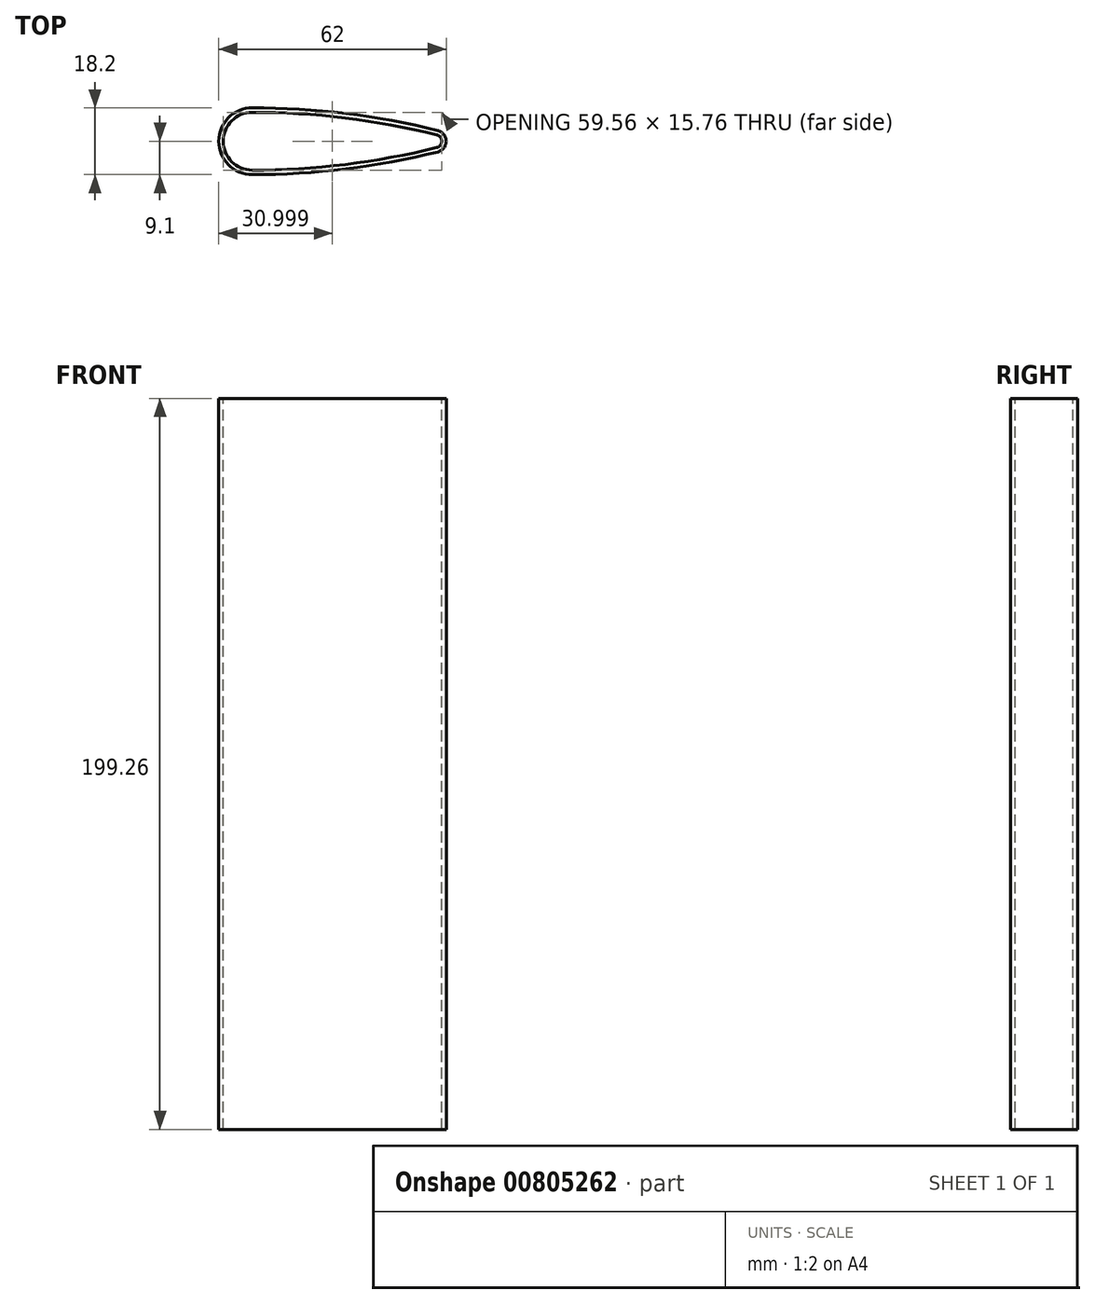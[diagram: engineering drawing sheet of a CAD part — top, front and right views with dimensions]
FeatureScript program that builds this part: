
annotation { "Feature Type Name" : "Feature", "Feature Type Description" : "" }
export const myFeature = defineFeature(function(context is Context, id is Id, definition is map)
    precondition{}
    {
        {
            var Q0;
            Q0=qCreatedBy(makeId("Front.planeOp"),FACE);
            var sketch = newSketch(context, id + "F0", { "sketchPlane" : qUnion([Q0])});
            skCircle(sketch, "E0", {"center": v(0, 0) * mm, "radius": 10 * mm});
            skLineSegment(sketch, "E1", {"start": v(-10, 0) * mm, "end": v(-10, 199.26) * mm});
            skSolve(sketch);
        }
        {
            var Q0;
            Q0=qCreatedBy(makeId("Top.planeOp"),FACE);
            var sketch = newSketch(context, id + "F1", { "sketchPlane" : qUnion([Q0])});
            skArc(sketch, "E2", {"start": v(-12.13, 9.1) * mm, "mid": v(-21.23, 0) * mm, "end": v(-12.13, -9.1) * mm});
            skLineSegment(sketch, "E3", {"start": v(-12.13, 0) * mm, "end": v(40.77, 0) * mm});
            skArc(sketch, "E4", {"start": v(38.5, -2.91) * mm, "mid": v(40.77, 0) * mm, "end": v(38.5, 2.91) * mm});
            skLineSegment(sketch, "E5", {"start": v(-12.13, 0) * mm, "end": v(-12.13, 9.1) * mm});
            skLineSegment(sketch, "E6", {"start": v(-12.13, 9.1) * mm, "end": v(10.82, 9.1) * mm});
            skArc(sketch, "E7", {"start": v(38.5, 2.91) * mm, "mid": v(13.37, 7.55) * mm, "end": v(-12.13, 9.1) * mm});
            skArc(sketch, "E8.MirrorCS", {"start": v(38.5, -2.91) * mm, "mid": v(13.37, -7.55) * mm, "end": v(-12.13, -9.1) * mm});
            skArc(sketch, "E9.0", {"start": v(38.2, 1.73) * mm, "mid": v(13.22, 6.34) * mm, "end": v(-12.13, 7.88) * mm});
            skArc(sketch, "E9.1", {"start": v(38.2, -1.73) * mm, "mid": v(13.22, -6.34) * mm, "end": v(-12.13, -7.88) * mm});
            skArc(sketch, "E9.2", {"start": v(-12.13, 7.88) * mm, "mid": v(-20.01, 0) * mm, "end": v(-12.13, -7.88) * mm});
            skArc(sketch, "E10", {"start": v(38.2, -1.73) * mm, "mid": v(39.55, 0) * mm, "end": v(38.2, 1.73) * mm});
            skSolve(sketch);
        }
        {
            var Q0;
            Q0=qCreatedBy(makeId("Top.planeOp"),FACE);
            var sketch = newSketch(context, id + "F2", { "sketchPlane" : qUnion([Q0])});
            skArc(sketch, "E11", {"start": v(-17.42, 11.17) * mm, "mid": v(-30.07, -1.48) * mm, "end": v(-17.42, -14.13) * mm});
            skLineSegment(sketch, "E12", {"start": v(-17.42, -1.48) * mm, "end": v(27.93, -1.48) * mm});
            skArc(sketch, "E13", {"start": v(25.9, -4.66) * mm, "mid": v(27.93, -1.48) * mm, "end": v(25.9, 1.7) * mm});
            skLineSegment(sketch, "E14", {"start": v(-17.42, -1.48) * mm, "end": v(-17.42, 11.17) * mm});
            skLineSegment(sketch, "E15", {"start": v(-17.42, 11.17) * mm, "end": v(-2.83, 11.17) * mm});
            skArc(sketch, "E16", {"start": v(25.9, 1.7) * mm, "mid": v(4.75, 8.77) * mm, "end": v(-17.42, 11.17) * mm});
            skArc(sketch, "E17.MirrorCS", {"start": v(25.9, -4.66) * mm, "mid": v(4.75, -11.74) * mm, "end": v(-17.42, -14.13) * mm});
            skArc(sketch, "E18.0", {"start": v(25.38, 0.59) * mm, "mid": v(4.49, 7.58) * mm, "end": v(-17.42, 9.95) * mm});
            skArc(sketch, "E18.1", {"start": v(25.38, -3.56) * mm, "mid": v(4.49, -10.55) * mm, "end": v(-17.42, -12.91) * mm});
            skArc(sketch, "E18.2", {"start": v(-17.42, 9.95) * mm, "mid": v(-28.85, -1.48) * mm, "end": v(-17.42, -12.91) * mm});
            skArc(sketch, "E19", {"start": v(25.38, -3.56) * mm, "mid": v(26.71, -1.48) * mm, "end": v(25.38, 0.59) * mm});
            skSolve(sketch);
        }
        {
            var Q0;
            {var subQ1=sQuery(id+"F1.wireOp",EDGE,"E2");Q0=makeQuery(id+"F1.imprint","IMPRINT",FACE,{"disambiguationData":[TD([[makeQuery(id+"F1.imprint","IMPRINT",EDGE,{"derivedFrom":subQ1}),1.0]])]});}
            var Q1;
            {var subQ0=sQuery(id+"F1.wireOp",EDGE,"E7");Q1=makeQuery(id+"F1.imprint","IMPRINT",FACE,{"disambiguationData":[TD([[makeQuery(id+"F1.imprint","IMPRINT",EDGE,{"derivedFrom":subQ0}),1.0]])]});}
            var Q2;
            Q2=sQuery(id+"F0.wireOp",EDGE,"E1");
            sweep(context, id + "F3", {"profiles" : qUnion([Q0, Q1]), "path" : qUnion([Q2])});
        }
    });
